# Revit family: rba-bim-B529
name_source: partatom
category: Plumbing Fixtures
revit_build: Autodesk Revit 2018 (Build: 20170223_1515(x64)
units: mm (PartAtom-declared; Revit-internal decimal feet)

## family parameters
Cut with Voids When Loaded = No
Host = Face
Part Type = Normal
Room Calculation Point = No
Round Connector Dimension = Use Diameter
Shared = Yes

## types (1)
- B-529
    ATS URL = http://www.atsspec.net
    Assembly Code = E1090100
    CW Connection = No
    CWFU = 0
    Default Elevation = 0 mm  [stored 0 ft]
    Description = Circular Waste Chute for Mounting in Countertops
    HW Connection = No
    HWFU = 0
    Height = 127 mm
    Installation Type = Counter Mounted
    Length = 140 mm
    Manufacturer = Bobrick Washroom Equipment, Inc.
    Materials and Finishes = Polished Finish Stainless Steel
    Model = B529
    Modified Issue = 20220323.01
    Price = Prices may vary. Please consult Manufacturer Representative for most up-to-date price list.
    Product Documentation Link = http://www.bobrick.com
    Product Page URL = http://www.bobrick.com
    URL = http://www.bobrick.com
    Vent Connection = No
    WFU = 0
    Waste Connection = No

note: [stored X ft] marks values corroborated as IEEE doubles in the binary element streams (Revit-internal decimal feet)

## geometry (parser evidence)
native form markers: Blend x2, Sweep x3
no freeform markers — native parametric forms only
